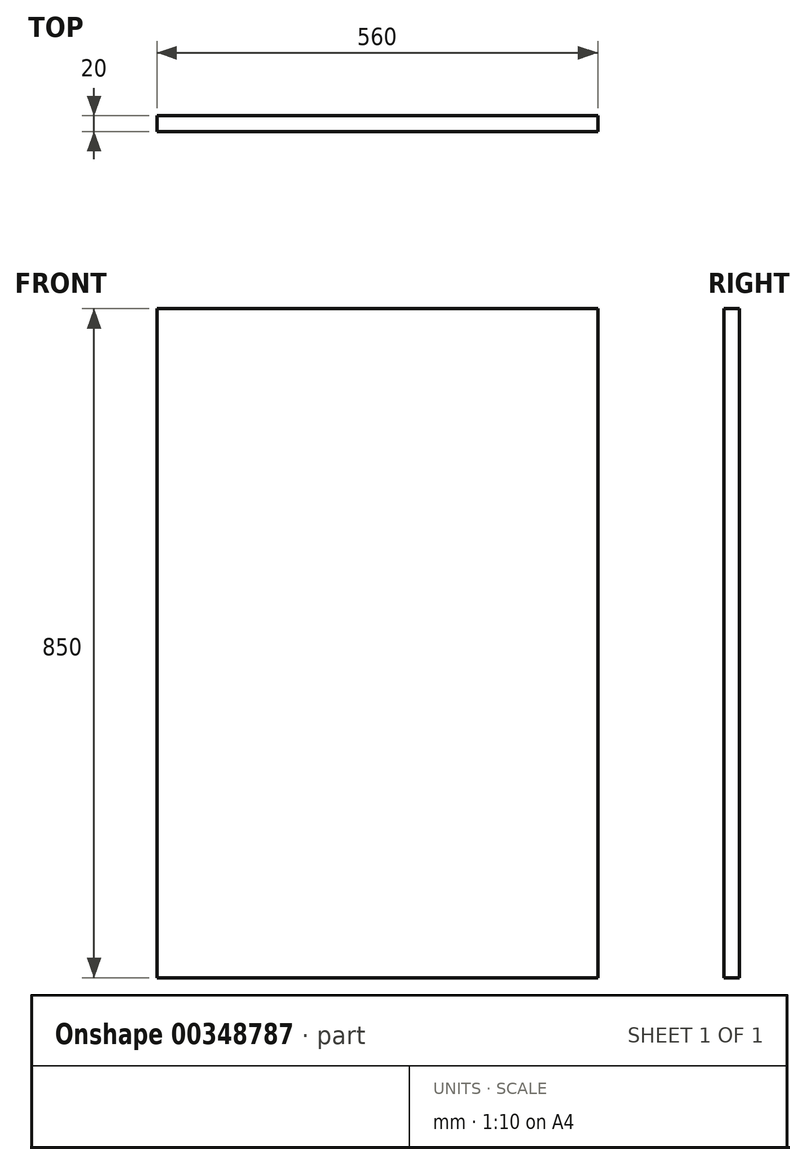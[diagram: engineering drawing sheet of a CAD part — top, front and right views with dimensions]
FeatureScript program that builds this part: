
annotation { "Feature Type Name" : "Feature", "Feature Type Description" : "" }
export const myFeature = defineFeature(function(context is Context, id is Id, definition is map)
    precondition{}
    {
        {
            var Q0;
            Q0=qCreatedBy(makeId("Front.planeOp"),FACE);
            var sketch = newSketch(context, id + "F0", { "sketchPlane" : qUnion([Q0])});
            skLineSegment(sketch, "E0.bottom", {"start": v(-560, -850) * mm, "end": v(0, -850) * mm});
            skLineSegment(sketch, "E0.top", {"start": v(-560, 0) * mm, "end": v(0, 0) * mm});
            skLineSegment(sketch, "E0.left", {"start": v(-560, -850) * mm, "end": v(-560, 0) * mm});
            skLineSegment(sketch, "E0.right", {"start": v(0, -850) * mm, "end": v(0, 0) * mm});
            skSolve(sketch);
        }
        {
            var Q0;
            Q0=qSketchRegion(id+"F0",true);
            extrude(context, id + "F1", {"entities" : qUnion([Q0]), "depth" : 20 * mm});
        }
    });
